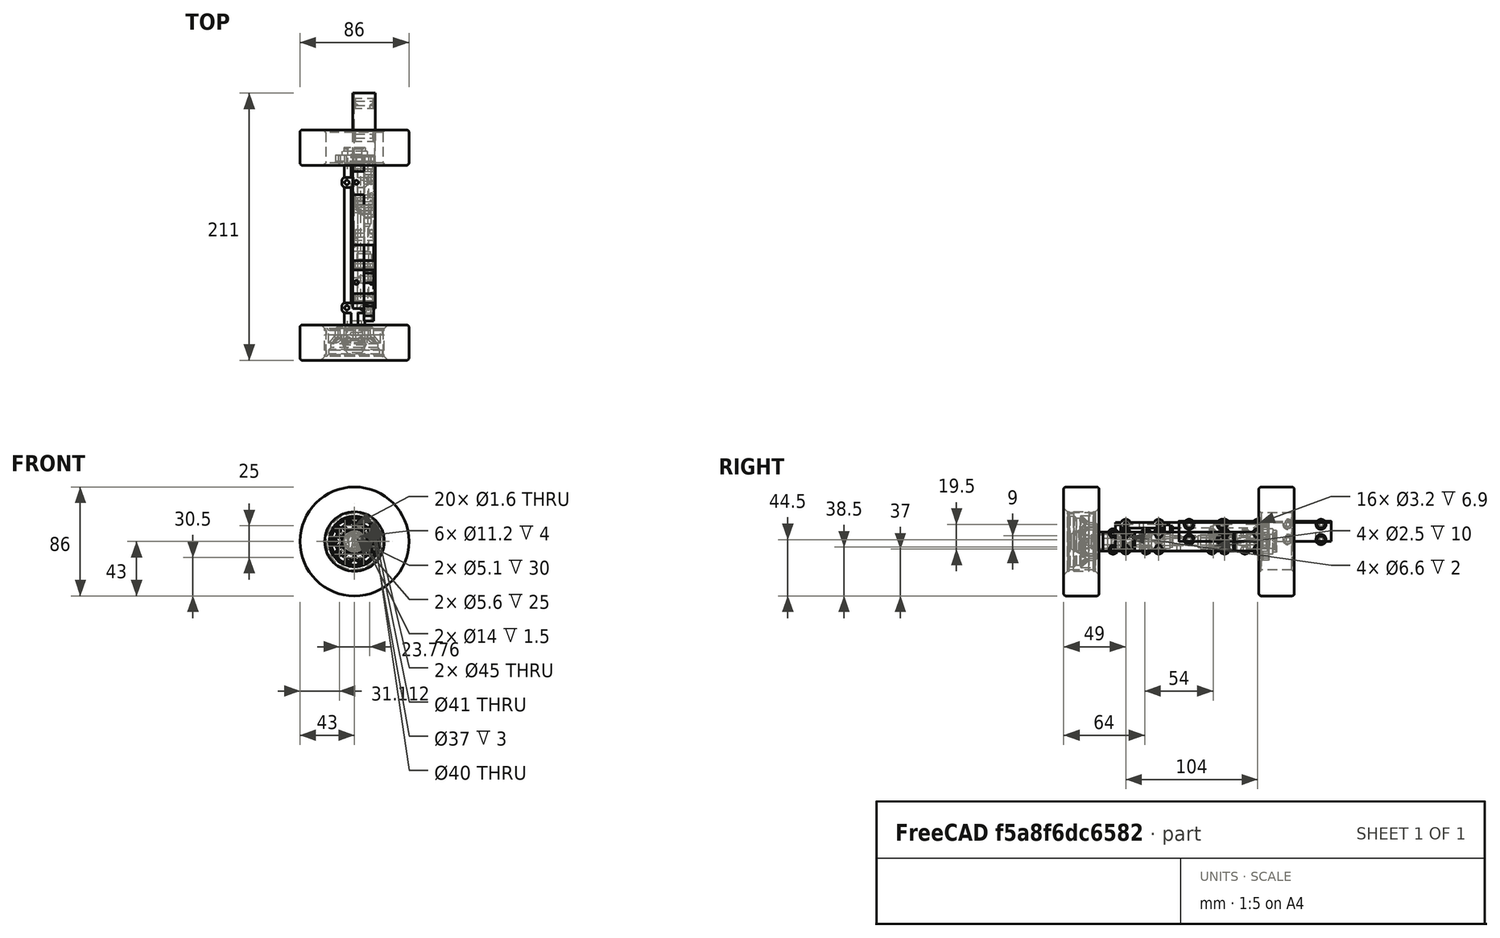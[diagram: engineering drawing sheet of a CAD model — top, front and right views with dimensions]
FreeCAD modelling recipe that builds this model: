
FCSTD DOCUMENT  (FreeCAD 0.19R)
Label: trailer-axle
License: CC-BY 3.0
LicenseURL: http://creativecommons.org/licenses/by/3.0/
objects: Part::Cylinder×133, Part::MultiFuse×123, Part::Cut×40, Part::Box×11, Part::Fillet×10, Part::Extrusion×8, Part::Chamfer×8, Part::Mirroring×5, Part::Feature×4, Part::Cone×3
note: 345 computed .brp shape members not serialized (recipe doc carries the construction recipe); baked Part::Feature solids carry a one-line shape summary decoded from their .brp

FEATURE [Part::Box] Box
  AttacherType = Attacher::AttachEngine3D
  Height = 15
  Length = 18
  Placement = pos=(-1.5,0,0) rot=(0,0,1;0rad)
  Width = 120
FEATURE [Part::Cylinder] Cylinder
  Angle = 360
  AttacherType = Attacher::AttachEngine3D
  Height = 18
  Placement = pos=(0,8,1.5) rot=(0,1,0;1.5708rad)
  Radius = 4
FEATURE [Part::Cylinder] Cylinder001
  Angle = 360
  AttacherType = Attacher::AttachEngine3D
  Height = 18
  Placement = pos=(0,8,13.5) rot=(0,1,0;1.5708rad)
  Radius = 4
FEATURE [Part::Cylinder] Cylinder002
  Angle = 360
  AttacherType = Attacher::AttachEngine3D
  Height = 18
  Placement = pos=(0,8,1.5) rot=(0,1,0;1.5708rad)
  Radius = 4
FEATURE [Part::Cylinder] Cylinder003
  Angle = 360
  AttacherType = Attacher::AttachEngine3D
  Height = 18
  Placement = pos=(0,8,13.5) rot=(0,1,0;1.5708rad)
  Radius = 4
FEATURE [Part::MultiFuse] Fusion009
  Refine = true
  Shapes = -> [Cylinder,Cylinder001]
FEATURE [Part::MultiFuse] Fusion010
  Placement = pos=(0,104,0) rot=(0,0,1;0rad)
  Refine = true
  Shapes = -> [Cylinder002,Cylinder003]
FEATURE [Part::MultiFuse] Fusion008
  Placement = pos=(-1.5,0,0) rot=(0,0,1;0rad)
  Refine = true
  Shapes = -> [Fusion009,Fusion010]
FEATURE [Part::Cylinder] Cylinder004
  Angle = 360
  AttacherType = Attacher::AttachEngine3D
  Height = 18
  Placement = pos=(0,8,1.5) rot=(0,1,0;1.5708rad)
  Radius = 1.6
FEATURE [Part::Cylinder] Cylinder005
  Angle = 360
  AttacherType = Attacher::AttachEngine3D
  Height = 18
  Placement = pos=(0,8,13.5) rot=(0,1,0;1.5708rad)
  Radius = 1.6
FEATURE [Part::Cylinder] Cylinder006
  Angle = 360
  AttacherType = Attacher::AttachEngine3D
  Height = 18
  Placement = pos=(0,8,1.5) rot=(0,1,0;1.5708rad)
  Radius = 1.6
FEATURE [Part::Cylinder] Cylinder007
  Angle = 360
  AttacherType = Attacher::AttachEngine3D
  Height = 18
  Placement = pos=(0,8,13.5) rot=(0,1,0;1.5708rad)
  Radius = 1.6
FEATURE [Part::MultiFuse] Fusion012
  Refine = true
  Shapes = -> [Cylinder004,Cylinder005]
FEATURE [Part::MultiFuse] Fusion013
  Placement = pos=(0,104,0) rot=(0,0,1;0rad)
  Refine = true
  Shapes = -> [Cylinder006,Cylinder007]
FEATURE [Part::MultiFuse] Fusion014
  Placement = pos=(-1.5,0,0) rot=(0,0,1;0rad)
  Refine = true
  Shapes = -> [Fusion012,Fusion013]
FEATURE [Part::Cylinder] Cylinder008
  Angle = 360
  AttacherType = Attacher::AttachEngine3D
  Height = 2
  Placement = pos=(0,8,1.5) rot=(0,1,0;1.5708rad)
  Radius = 3.3
FEATURE [Part::Cylinder] Cylinder009
  Angle = 360
  AttacherType = Attacher::AttachEngine3D
  Height = 2
  Placement = pos=(0,8,13.5) rot=(0,1,0;1.5708rad)
  Radius = 3.1
FEATURE [Part::MultiFuse] Fusion015
  Refine = true
  Shapes = -> [Cylinder009,Cylinder008]
FEATURE [Part::Cylinder] Cylinder010
  Angle = 360
  AttacherType = Attacher::AttachEngine3D
  Height = 2
  Placement = pos=(0,8,13.5) rot=(0,1,0;1.5708rad)
  Radius = 3.1
FEATURE [Part::Cylinder] Cylinder011
  Angle = 360
  AttacherType = Attacher::AttachEngine3D
  Height = 2
  Placement = pos=(0,8,1.5) rot=(0,1,0;1.5708rad)
  Radius = 3.3
FEATURE [Part::MultiFuse] Fusion016
  Placement = pos=(0,104,0) rot=(0,0,1;0rad)
  Refine = true
  Shapes = -> [Cylinder010,Cylinder011]
FEATURE [Part::MultiFuse] Fusion018
  Placement = pos=(-1.5,0,0) rot=(0,0,1;0rad)
  Refine = true
  Shapes = -> [Fusion015,Fusion016]
FEATURE [Part::Feature] Face
  Placement = pos=(-1,8,1.5) rot=(0.250563,0.935113,0.250563;1.63783rad)
  shape: bbox 2e-07 x 9.017 x 9.331 mm, 1 faces, 0 solids (baked)
FEATURE [Part::Extrusion] Extrude
  Base = -> Face
  Dir = (2,0,0)
  DirMode = 0
  FaceMakerClass = Part::FaceMakerExtrusion
  LengthFwd = 0
  LengthRev = 0
  Placement = pos=(-2,0,0) rot=(0,0,1;0rad)
  Solid = false
  Symmetric = false
FEATURE [Part::Feature] Face001
  Placement = pos=(-1,8,1.5) rot=(0.250563,0.935113,0.250563;1.63783rad)
  shape: bbox 2e-07 x 9.017 x 9.331 mm, 1 faces, 0 solids (baked)
FEATURE [Part::Extrusion] Extrude001
  Base = -> Face001
  Dir = (2,0,0)
  DirMode = 0
  FaceMakerClass = Part::FaceMakerExtrusion
  LengthFwd = 0
  LengthRev = 0
  Placement = pos=(-2,0,12) rot=(0,0,1;0rad)
  Solid = false
  Symmetric = false
FEATURE [Part::MultiFuse] Fusion019
  Refine = true
  Shapes = -> [Extrude001,Extrude]
FEATURE [Part::Extrusion] Extrude002
  Base = -> Face
  Dir = (2,0,0)
  DirMode = 0
  FaceMakerClass = Part::FaceMakerExtrusion
  LengthFwd = 0
  LengthRev = 0
  Placement = pos=(-2,0,0) rot=(0,0,1;0rad)
  Solid = false
  Symmetric = false
FEATURE [Part::Extrusion] Extrude003
  Base = -> Face001
  Dir = (2,0,0)
  DirMode = 0
  FaceMakerClass = Part::FaceMakerExtrusion
  LengthFwd = 0
  LengthRev = 0
  Placement = pos=(-2,0,12) rot=(0,0,1;0rad)
  Solid = false
  Symmetric = false
FEATURE [Part::MultiFuse] Fusion020
  Placement = pos=(0,104,0) rot=(0,0,1;0rad)
  Refine = true
  Shapes = -> [Extrude003,Extrude002]
FEATURE [Part::MultiFuse] Fusion021
  Placement = pos=(1.5,0,0) rot=(0,0,1;0rad)
  Refine = true
  Shapes = -> [Fusion020,Fusion019]
FEATURE [Part::Cylinder] Cylinder014
  Angle = 360
  AttacherType = Attacher::AttachEngine3D
  Height = 15
  Placement = pos=(12,0,0) rot=(0,0,1;0rad)
  Radius = 1.6
FEATURE [Part::Cylinder] Cylinder015
  Angle = 360
  AttacherType = Attacher::AttachEngine3D
  Height = 15
  Radius = 1.6
FEATURE [Part::MultiFuse] Fusion024
  Placement = pos=(1.5,20.5,0) rot=(0,0,1;0rad)
  Refine = true
  Shapes = -> [Cylinder014,Cylinder015]
FEATURE [Part::Cylinder] Cylinder018
  Angle = 360
  AttacherType = Attacher::AttachEngine3D
  Height = 15
  Placement = pos=(12,0,0) rot=(0,0,1;0rad)
  Radius = 1.6
FEATURE [Part::Cylinder] Cylinder019
  Angle = 360
  AttacherType = Attacher::AttachEngine3D
  Height = 15
  Radius = 1.6
FEATURE [Part::MultiFuse] Fusion030
  Placement = pos=(1.5,99.5,0) rot=(0,0,1;0rad)
  Refine = true
  Shapes = -> [Cylinder018,Cylinder019]
FEATURE [Part::MultiFuse] Fusion031
  Refine = true
  Shapes = -> [Fusion024,Fusion030]
FEATURE [Part::MultiFuse] Fusion032
  Placement = pos=(0,78,0) rot=(0,0,1;0rad)
  Refine = true
  Shapes = -> [Extrude003,Extrude002]
FEATURE [Part::MultiFuse] Fusion034
  Placement = pos=(0,26,0) rot=(0,0,1;0rad)
  Refine = true
  Shapes = -> [Extrude001,Extrude]
FEATURE [Part::MultiFuse] Fusion035
  Placement = pos=(0,26,0) rot=(0,0,1;0rad)
  Refine = true
  Shapes = -> [Cylinder009,Cylinder008]
FEATURE [Part::MultiFuse] Fusion036
  Placement = pos=(0,78,0) rot=(0,0,1;0rad)
  Refine = true
  Shapes = -> [Cylinder010,Cylinder011]
FEATURE [Part::MultiFuse] Fusion037
  Placement = pos=(-1.5,0,0) rot=(0,0,1;0rad)
  Refine = true
  Shapes = -> [Fusion035,Fusion036]
FEATURE [Part::MultiFuse] Fusion038
  Placement = pos=(1.5,0,0) rot=(0,0,1;0rad)
  Refine = true
  Shapes = -> [Fusion032,Fusion034]
FEATURE [Part::MultiFuse] Fusion039
  Placement = pos=(0,26,0) rot=(0,0,1;0rad)
  Refine = true
  Shapes = -> [Cylinder,Cylinder001]
FEATURE [Part::MultiFuse] Fusion040
  Placement = pos=(0,78,0) rot=(0,0,1;0rad)
  Refine = true
  Shapes = -> [Cylinder002,Cylinder003]
FEATURE [Part::MultiFuse] Fusion041
  Placement = pos=(-1.5,0,0) rot=(0,0,1;0rad)
  Refine = true
  Shapes = -> [Fusion040,Fusion039]
FEATURE [Part::MultiFuse] Fusion043
  Placement = pos=(0,78,0) rot=(0,0,1;0rad)
  Refine = true
  Shapes = -> [Cylinder006,Cylinder007]
FEATURE [Part::MultiFuse] Fusion044
  Placement = pos=(0,26,0) rot=(0,0,1;0rad)
  Refine = true
  Shapes = -> [Cylinder004,Cylinder005]
FEATURE [Part::MultiFuse] Fusion045
  Placement = pos=(-1.5,0,0) rot=(0,0,1;0rad)
  Refine = true
  Shapes = -> [Fusion043,Fusion044]
FEATURE [Part::Cylinder] Cylinder020
  Angle = 360
  AttacherType = Attacher::AttachEngine3D
  Height = 130
  Placement = pos=(7.5,125,7.5) rot=(1,0,0;1.5708rad)
  Radius = 3.5
FEATURE [Part::Cut] Cut008
  Refine = true
  Tool = -> Cylinder020
FEATURE [Part::Cylinder] Cylinder021
  Angle = 360
  AttacherType = Attacher::AttachEngine3D
  Height = 4
  Placement = pos=(7.5,4,20) rot=(1,0,0;1.5708rad)
  Radius = 5.6
FEATURE [Part::Cylinder] Cylinder022
  Angle = 360
  AttacherType = Attacher::AttachEngine3D
  Height = 2
  Placement = pos=(7.5,45,20) rot=(1,0,0;1.5708rad)
  Radius = 4.7
FEATURE [Part::Cylinder] Cylinder023
  Angle = 360
  AttacherType = Attacher::AttachEngine3D
  Height = 4.5
  Placement = pos=(7.5,43,20) rot=(1,0,0;1.5708rad)
  Radius = 5.6
FEATURE [Part::MultiFuse] Fusion047
  Refine = true
  Shapes = -> [Cylinder021,Cylinder023,Cylinder022]
FEATURE [Part::Cylinder] Cylinder024
  Angle = 360
  AttacherType = Attacher::AttachEngine3D
  Height = 2
  Placement = pos=(7.5,45,20) rot=(1,0,0;1.5708rad)
  Radius = 4.7
FEATURE [Part::Cylinder] Cylinder025
  Angle = 360
  AttacherType = Attacher::AttachEngine3D
  Height = 4
  Placement = pos=(7.5,4,20) rot=(1,0,0;1.5708rad)
  Radius = 5.6
FEATURE [Part::Cylinder] Cylinder026
  Angle = 360
  AttacherType = Attacher::AttachEngine3D
  Height = 4.5
  Placement = pos=(7.5,43,20) rot=(1,0,0;1.5708rad)
  Radius = 5.6
FEATURE [Part::MultiFuse] Fusion048
  Placement = pos=(15,120,0) rot=(0,0,1;3.14159rad)
  Refine = true
  Shapes = -> [Cylinder025,Cylinder026,Cylinder024]
FEATURE [Part::MultiFuse] Fusion049
  Placement = pos=(0,0,-12.5) rot=(0,0,1;0rad)
  Refine = true
  Shapes = -> [Fusion047,Fusion048]
FEATURE [Part::Cut] Cut009
  Base = -> Cut008
  Refine = true
  Tool = -> Fusion049
FEATURE [Part::Box] Box007
  AttacherType = Attacher::AttachEngine3D
  Height = 30
  Length = 10
  Placement = pos=(-2.5,0,-7) rot=(0,0,1;0rad)
  Width = 120
FEATURE [Part::Box] Box008
  AttacherType = Attacher::AttachEngine3D
  Height = 30
  Length = 10
  Placement = pos=(7.5,0,-7) rot=(0,0,1;0rad)
  Width = 120
FEATURE [Part::MultiFuse] Fusion050
  Placement = pos=(0,0,-12.5) rot=(0,0,1;0rad)
  Refine = true
  Shapes = -> [Fusion047,Fusion048]
FEATURE [Part::Cut] Cut012
  Base = -> Cut009
  Placement = pos=(0,-60,-7.5) rot=(0,0,1;0rad)
  Refine = true
  Tool = -> Box007
FEATURE [Part::Cut] Cut
  Base = -> Box
  Refine = true
  Tool = -> Fusion031
FEATURE [Part::MultiFuse] Fusion
  Refine = true
  Shapes = -> [Fusion041,Fusion008,Cut]
FEATURE [Part::MultiFuse] Fusion051
  Refine = true
  Shapes = -> [Fusion014,Fusion045]
FEATURE [Part::MultiFuse] Fusion052
  Refine = true
  Shapes = -> [Fusion018,Fusion021,Fusion037,Fusion038]
FEATURE [Part::MultiFuse] Fusion053
  Refine = true
  Shapes = -> [Fusion051,Fusion052]
FEATURE [Part::Cut] Cut013
  Base = -> Fusion
  Refine = true
  Tool = -> Fusion053
FEATURE [Part::Cylinder] Cylinder027
  Angle = 360
  AttacherType = Attacher::AttachEngine3D
  Height = 120
  Placement = pos=(7.5,120,7.5) rot=(1,0,0;1.5708rad)
  Radius = 3
FEATURE [Part::MultiFuse] Fusion054
  Refine = true
  Shapes = -> [Cylinder027,Fusion050]
FEATURE [Part::Cut] Cut014
  Base = -> Cut013
  Refine = true
  Tool = -> Fusion054
FEATURE [Part::MultiFuse] Fusion055
  Refine = true
  Shapes = -> [Cylinder027,Fusion050]
FEATURE [Part::Cut] Cut016
  Base = -> Fusion
  Refine = true
  Tool = -> Fusion053
FEATURE [Part::Cut] Cut015
  Base = -> Cut016
  Refine = true
  Tool = -> Fusion055
FEATURE [Part::Box] Box009
  AttacherType = Attacher::AttachEngine3D
  Height = 30
  Length = 10
  Placement = pos=(-2.5,0,-7) rot=(0,0,1;0rad)
  Width = 120
FEATURE [Part::Cut] Cut017
  Base = -> Cut014
  Refine = true
  Tool = -> Box008
FEATURE [Part::Cut] Cut018
  Base = -> Cut015
  Refine = true
  Tool = -> Box009
FEATURE [Part::Cylinder] Cylinder028
  Angle = 360
  AttacherType = Attacher::AttachEngine3D
  Height = 0.1
  Placement = pos=(0.5,8,1.5) rot=(0,1,0;1.5708rad)
  Radius = 1.6
FEATURE [Part::Cylinder] Cylinder029
  Angle = 360
  AttacherType = Attacher::AttachEngine3D
  Height = 0.1
  Placement = pos=(0.5,8,13.5) rot=(0,1,0;1.5708rad)
  Radius = 1.6
FEATURE [Part::MultiFuse] Fusion056
  Refine = true
  Shapes = -> [Cylinder029,Cylinder028]
FEATURE [Part::Cylinder] Cylinder030
  Angle = 360
  AttacherType = Attacher::AttachEngine3D
  Height = 0.1
  Placement = pos=(0.5,8,13.5) rot=(0,1,0;1.5708rad)
  Radius = 1.6
FEATURE [Part::Cylinder] Cylinder031
  Angle = 360
  AttacherType = Attacher::AttachEngine3D
  Height = 0.1
  Placement = pos=(0.5,8,1.5) rot=(0,1,0;1.5708rad)
  Radius = 1.6
FEATURE [Part::MultiFuse] Fusion057
  Placement = pos=(0,26,0) rot=(0,0,1;0rad)
  Refine = true
  Shapes = -> [Cylinder030,Cylinder031]
FEATURE [Part::MultiFuse] Fusion058
  Refine = true
  Shapes = -> [Fusion056,Fusion057]
FEATURE [Part::MultiFuse] Fusion059
  Placement = pos=(0,26,0) rot=(0,0,1;0rad)
  Refine = true
  Shapes = -> [Cylinder030,Cylinder031]
FEATURE [Part::MultiFuse] Fusion060
  Refine = true
  Shapes = -> [Cylinder029,Cylinder028]
FEATURE [Part::MultiFuse] Fusion061
  Placement = pos=(0,78,0) rot=(0,0,1;0rad)
  Refine = true
  Shapes = -> [Fusion060,Fusion059]
FEATURE [Part::MultiFuse] Fusion062
  Refine = true
  Shapes = -> [Fusion061,Fusion058]
FEATURE [Part::MultiFuse] Fusion063
  Refine = true
  Shapes = -> [Fusion056,Fusion057]
FEATURE [Part::MultiFuse] Fusion065
  Placement = pos=(0,78,0) rot=(0,0,1;0rad)
  Refine = true
  Shapes = -> [Fusion060,Fusion059]
FEATURE [Part::MultiFuse] Fusion064
  Placement = pos=(13.9,0,0) rot=(0,0,1;0rad)
  Refine = true
  Shapes = -> [Fusion065,Fusion063]
FEATURE [Part::MultiFuse] Fusion066
  Placement = pos=(0,-50,0) rot=(0,0,1;0rad)
  Refine = true
  Shapes = -> [Cut017,Fusion062]
FEATURE [Part::MultiFuse] Fusion067
  Placement = pos=(0,-50,-7.5) rot=(0,0,1;0rad)
  Refine = true
  Shapes = -> [Fusion064,Cut018]
FEATURE [Part::Cylinder] Cylinder032
  Angle = 360
  AttacherType = Attacher::AttachEngine3D
  Height = 15
  Placement = pos=(12,0,0) rot=(0,0,1;0rad)
  Radius = 1.6
FEATURE [Part::Cylinder] Cylinder033
  Angle = 360
  AttacherType = Attacher::AttachEngine3D
  Height = 15
  Radius = 1.6
FEATURE [Part::MultiFuse] Fusion068
  Placement = pos=(1.5,10.5,0) rot=(0,0,1;0rad)
  Refine = true
  Shapes = -> [Cylinder032,Cylinder033]
FEATURE [Part::Cylinder] Cylinder034
  Angle = 360
  AttacherType = Attacher::AttachEngine3D
  Height = 15
  Placement = pos=(12,0,0) rot=(0,0,1;0rad)
  Radius = 1.6
FEATURE [Part::Cylinder] Cylinder035
  Angle = 360
  AttacherType = Attacher::AttachEngine3D
  Height = 15
  Radius = 1.6
FEATURE [Part::MultiFuse] Fusion069
  Placement = pos=(1.5,109.5,0) rot=(0,0,1;0rad)
  Refine = true
  Shapes = -> [Cylinder034,Cylinder035]
FEATURE [Part::Feature] Face002
  Placement = pos=(-1,8,1.5) rot=(0.250563,0.935113,0.250563;1.63783rad)
  shape: bbox 2e-07 x 9.017 x 9.331 mm, 1 faces, 0 solids (baked)
FEATURE [Part::Cylinder] Cylinder036
  Angle = 360
  AttacherType = Attacher::AttachEngine3D
  Height = 18
  Placement = pos=(0,8,1.5) rot=(0,1,0;1.5708rad)
  Radius = 1.6
FEATURE [Part::Cylinder] Cylinder037
  Angle = 360
  AttacherType = Attacher::AttachEngine3D
  Height = 18
  Placement = pos=(0,8,13.5) rot=(0,1,0;1.5708rad)
  Radius = 1.6
FEATURE [Part::MultiFuse] Fusion072
  Refine = true
  Shapes = -> [Cylinder036,Cylinder037]
FEATURE [Part::Cylinder] Cylinder038
  Angle = 360
  AttacherType = Attacher::AttachEngine3D
  Height = 18
  Placement = pos=(0,8,1.5) rot=(0,1,0;1.5708rad)
  Radius = 1.6
FEATURE [Part::Cylinder] Cylinder039
  Angle = 360
  AttacherType = Attacher::AttachEngine3D
  Height = 18
  Placement = pos=(0,8,13.5) rot=(0,1,0;1.5708rad)
  Radius = 1.6
FEATURE [Part::MultiFuse] Fusion073
  Placement = pos=(0,104,0) rot=(0,0,1;0rad)
  Refine = true
  Shapes = -> [Cylinder038,Cylinder039]
FEATURE [Part::MultiFuse] Fusion070
  Placement = pos=(-1.5,0,0) rot=(0,0,1;0rad)
  Refine = true
  Shapes = -> [Fusion072,Fusion073]
FEATURE [Part::Cylinder] Cylinder040
  Angle = 360
  AttacherType = Attacher::AttachEngine3D
  Height = 2
  Placement = pos=(0,8,1.5) rot=(0,1,0;1.5708rad)
  Radius = 3.3
FEATURE [Part::Cylinder] Cylinder041
  Angle = 360
  AttacherType = Attacher::AttachEngine3D
  Height = 2
  Placement = pos=(0,8,13.5) rot=(0,1,0;1.5708rad)
  Radius = 3.1
FEATURE [Part::MultiFuse] Fusion071
  Refine = true
  Shapes = -> [Cylinder041,Cylinder040]
FEATURE [Part::Cylinder] Cylinder042
  Angle = 360
  AttacherType = Attacher::AttachEngine3D
  Height = 2
  Placement = pos=(0,8,13.5) rot=(0,1,0;1.5708rad)
  Radius = 3.1
FEATURE [Part::Cylinder] Cylinder043
  Angle = 360
  AttacherType = Attacher::AttachEngine3D
  Height = 2
  Placement = pos=(0,8,1.5) rot=(0,1,0;1.5708rad)
  Radius = 3.3
FEATURE [Part::MultiFuse] Fusion074
  Placement = pos=(0,104,0) rot=(0,0,1;0rad)
  Refine = true
  Shapes = -> [Cylinder042,Cylinder043]
FEATURE [Part::MultiFuse] Fusion075
  Placement = pos=(-1.5,0,0) rot=(0,0,1;0rad)
  Refine = true
  Shapes = -> [Fusion071,Fusion074]
FEATURE [Part::Extrusion] Extrude004
  Base = -> Face002
  Dir = (2,0,0)
  DirMode = 0
  FaceMakerClass = Part::FaceMakerExtrusion
  LengthFwd = 0
  LengthRev = 0
  Placement = pos=(-2,0,0) rot=(0,0,1;0rad)
  Solid = false
  Symmetric = false
FEATURE [Part::Feature] Face003
  Placement = pos=(-1,8,1.5) rot=(0.250563,0.935113,0.250563;1.63783rad)
  shape: bbox 2e-07 x 9.017 x 9.331 mm, 1 faces, 0 solids (baked)
FEATURE [Part::Extrusion] Extrude005
  Base = -> Face003
  Dir = (2,0,0)
  DirMode = 0
  FaceMakerClass = Part::FaceMakerExtrusion
  LengthFwd = 0
  LengthRev = 0
  Placement = pos=(-2,0,12) rot=(0,0,1;0rad)
  Solid = false
  Symmetric = false
FEATURE [Part::MultiFuse] Fusion076
  Refine = true
  Shapes = -> [Extrude005,Extrude004]
FEATURE [Part::Extrusion] Extrude006
  Base = -> Face002
  Dir = (2,0,0)
  DirMode = 0
  FaceMakerClass = Part::FaceMakerExtrusion
  LengthFwd = 0
  LengthRev = 0
  Placement = pos=(-2,0,0) rot=(0,0,1;0rad)
  Solid = false
  Symmetric = false
FEATURE [Part::Extrusion] Extrude007
  Base = -> Face003
  Dir = (2,0,0)
  DirMode = 0
  FaceMakerClass = Part::FaceMakerExtrusion
  LengthFwd = 0
  LengthRev = 0
  Placement = pos=(-2,0,12) rot=(0,0,1;0rad)
  Solid = false
  Symmetric = false
FEATURE [Part::MultiFuse] Fusion077
  Placement = pos=(0,104,0) rot=(0,0,1;0rad)
  Refine = true
  Shapes = -> [Extrude007,Extrude006]
FEATURE [Part::MultiFuse] Fusion078
  Placement = pos=(1.5,0,0) rot=(0,0,1;0rad)
  Refine = true
  Shapes = -> [Fusion077,Fusion076]
FEATURE [Part::MultiFuse] Fusion079
  Placement = pos=(0,78,0) rot=(0,0,1;0rad)
  Refine = true
  Shapes = -> [Extrude007,Extrude006]
FEATURE [Part::MultiFuse] Fusion080
  Placement = pos=(0,26,0) rot=(0,0,1;0rad)
  Refine = true
  Shapes = -> [Extrude005,Extrude004]
FEATURE [Part::MultiFuse] Fusion081
  Placement = pos=(0,26,0) rot=(0,0,1;0rad)
  Refine = true
  Shapes = -> [Cylinder041,Cylinder040]
FEATURE [Part::MultiFuse] Fusion082
  Placement = pos=(0,78,0) rot=(0,0,1;0rad)
  Refine = true
  Shapes = -> [Cylinder042,Cylinder043]
FEATURE [Part::MultiFuse] Fusion083
  Placement = pos=(-1.5,0,0) rot=(0,0,1;0rad)
  Refine = true
  Shapes = -> [Fusion081,Fusion082]
FEATURE [Part::MultiFuse] Fusion084
  Placement = pos=(1.5,0,0) rot=(0,0,1;0rad)
  Refine = true
  Shapes = -> [Fusion079,Fusion080]
FEATURE [Part::MultiFuse] Fusion085
  Placement = pos=(0,78,0) rot=(0,0,1;0rad)
  Refine = true
  Shapes = -> [Cylinder038,Cylinder039]
FEATURE [Part::MultiFuse] Fusion086
  Placement = pos=(0,26,0) rot=(0,0,1;0rad)
  Refine = true
  Shapes = -> [Cylinder036,Cylinder037]
FEATURE [Part::MultiFuse] Fusion087
  Placement = pos=(-1.5,0,0) rot=(0,0,1;0rad)
  Refine = true
  Shapes = -> [Fusion085,Fusion086]
FEATURE [Part::MultiFuse] Fusion088
  Refine = true
  Shapes = -> [Fusion070,Fusion087]
FEATURE [Part::MultiFuse] Fusion089
  Refine = true
  Shapes = -> [Fusion075,Fusion078,Fusion083,Fusion084]
FEATURE [Part::MultiFuse] Fusion090
  Refine = true
  Shapes = -> [Fusion088,Fusion089]
FEATURE [Part::Cylinder] Cylinder044
  Angle = 360
  AttacherType = Attacher::AttachEngine3D
  Height = 18
  Placement = pos=(0,8,1.5) rot=(0,1,0;1.5708rad)
  Radius = 4
FEATURE [Part::Cylinder] Cylinder045
  Angle = 360
  AttacherType = Attacher::AttachEngine3D
  Height = 18
  Placement = pos=(0,8,13.5) rot=(0,1,0;1.5708rad)
  Radius = 4
FEATURE [Part::MultiFuse] Fusion093
  Refine = true
  Shapes = -> [Cylinder044,Cylinder045]
FEATURE [Part::Cylinder] Cylinder046
  Angle = 360
  AttacherType = Attacher::AttachEngine3D
  Height = 18
  Placement = pos=(0,8,1.5) rot=(0,1,0;1.5708rad)
  Radius = 4
FEATURE [Part::Cylinder] Cylinder047
  Angle = 360
  AttacherType = Attacher::AttachEngine3D
  Height = 18
  Placement = pos=(0,8,13.5) rot=(0,1,0;1.5708rad)
  Radius = 4
FEATURE [Part::MultiFuse] Fusion092
  Placement = pos=(0,104,0) rot=(0,0,1;0rad)
  Refine = true
  Shapes = -> [Cylinder046,Cylinder047]
FEATURE [Part::MultiFuse] Fusion091
  Placement = pos=(-1.5,0,0) rot=(0,0,1;0rad)
  Refine = true
  Shapes = -> [Fusion093,Fusion092]
FEATURE [Part::MultiFuse] Fusion094
  Placement = pos=(0,26,0) rot=(0,0,1;0rad)
  Refine = true
  Shapes = -> [Cylinder044,Cylinder045]
FEATURE [Part::MultiFuse] Fusion095
  Placement = pos=(0,78,0) rot=(0,0,1;0rad)
  Refine = true
  Shapes = -> [Cylinder046,Cylinder047]
FEATURE [Part::MultiFuse] Fusion096
  Placement = pos=(-1.5,0,0) rot=(0,0,1;0rad)
  Refine = true
  Shapes = -> [Fusion095,Fusion094]
FEATURE [Part::Box] Box010
  AttacherType = Attacher::AttachEngine3D
  Height = 15
  Length = 18
  Placement = pos=(-1.5,0,0) rot=(0,0,1;0rad)
  Width = 120
FEATURE [Part::Cylinder] Cylinder048
  Angle = 360
  AttacherType = Attacher::AttachEngine3D
  Height = 120
  Placement = pos=(8,0,8) rot=(-1,0,0;1.5708rad)
  Radius = 8
FEATURE [Part::Cylinder] Cylinder049
  Angle = 360
  AttacherType = Attacher::AttachEngine3D
  Height = 28
  Placement = pos=(0,0,0) rot=(1,0,0;1.5708rad)
  Radius = 43
FEATURE [Part::Cylinder] Cylinder050
  Angle = 360
  AttacherType = Attacher::AttachEngine3D
  Height = 28
  Placement = pos=(0,0,0) rot=(1,0,0;1.5708rad)
  Radius = 22.5
FEATURE [Part::Cut] Cut019
  Base = -> Cylinder049
  Refine = true
  Tool = -> Cylinder050
FEATURE [Part::Cylinder] Cylinder051
  Angle = 360
  AttacherType = Attacher::AttachEngine3D
  Height = 28
  Placement = pos=(0,0,0) rot=(1,0,0;1.5708rad)
  Radius = 43
FEATURE [Part::Cylinder] Cylinder052
  Angle = 360
  AttacherType = Attacher::AttachEngine3D
  Height = 28
  Placement = pos=(0,0,0) rot=(1,0,0;1.5708rad)
  Radius = 22.5
FEATURE [Part::Cut] Cut020
  Base = -> Cylinder051
  Refine = true
  Tool = -> Cylinder052
FEATURE [Part::Fillet] Fillet003
  Base = -> Cut020
  Edges = 2 edges r=2: [Edge1,Edge3]
FEATURE [Part::Chamfer] Chamfer001
  Base = -> Fillet003
  Edges = 2 edges r=2: [Edge8,Edge9]
FEATURE [Part::Fillet] Fillet002  label="wheel-wide-right"
  Base = -> Chamfer001
  Edges = 2 edges r=3: [Edge1,Edge12]
  Placement = pos=(0,91,0) rot=(0,0,1;0rad)
FEATURE [Part::Cylinder] Cylinder073
  Angle = 360
  AttacherType = Attacher::AttachEngine3D
  Height = 22
  Radius = 23.5
FEATURE [Part::Cone] Cone002
  Angle = 360
  AttacherType = Attacher::AttachEngine3D
  Height = 7
  Placement = pos=(0,0,15) rot=(0,0,1;0rad)
  Radius1 = 21
  Radius2 = 15
FEATURE [Part::Cylinder] Cylinder081
  Angle = 360
  AttacherType = Attacher::AttachEngine3D
  Height = 26
  Radius = 10
FEATURE [Part::Cylinder] Cylinder078
  Angle = 360
  AttacherType = Attacher::AttachEngine3D
  Height = 22
  Radius = 18.5
FEATURE [Part::Cylinder] Cylinder074
  Angle = 360
  AttacherType = Attacher::AttachEngine3D
  Height = 19
  Radius = 23.5
FEATURE [Part::Cut] Cut027
  Base = -> Cone002
  Refine = true
  Tool = -> Cylinder081
FEATURE [Part::Cylinder] Cylinder077
  Angle = 360
  AttacherType = Attacher::AttachEngine3D
  Height = 12
  Placement = pos=(0,0,0.5) rot=(0,0,1;0rad)
  Radius = 23.5
FEATURE [Part::Cylinder] Cylinder084
  Angle = 360
  AttacherType = Attacher::AttachEngine3D
  Height = 8
  Placement = pos=(12,0,16) rot=(0,1,0;1.01229rad)
  Radius = 2.5
FEATURE [Part::Cylinder] Cylinder085
  Angle = 360
  AttacherType = Attacher::AttachEngine3D
  Height = 8
  Placement = pos=(12,0,16) rot=(0,1,0;1.01229rad)
  Radius = 2.5
FEATURE [Part::Mirroring] Part__Mirroring006  label="Cylinder107 (Mirror #1)010"
  Base = (0,0,0)
  Normal = (0,0,1)
  Source = -> Cylinder085
FEATURE [Part::MultiFuse] Fusion097
  Placement = pos=(0,0,0) rot=(0,0,1;0.628319rad)
  Refine = true
  Shapes = -> [Cylinder084,Part__Mirroring006]
FEATURE [Part::Cylinder] Cylinder075
  Angle = 360
  AttacherType = Attacher::AttachEngine3D
  Height = 19
  Radius = 22.1
FEATURE [Part::Cut] Cut022
  Base = -> Cylinder074
  Placement = pos=(0,0,1.5) rot=(0,0,1;0rad)
  Refine = true
  Tool = -> Cylinder075
FEATURE [Part::Cut] Cut023
  Base = -> Cylinder073
  Refine = true
  Tool = -> Cut022
FEATURE [Part::Cylinder] Cylinder076
  Angle = 360
  AttacherType = Attacher::AttachEngine3D
  Height = 12
  Radius = 22
FEATURE [Part::Cut] Cut024
  Base = -> Cylinder077
  Placement = pos=(0,0,4.5) rot=(0,0,1;0rad)
  Refine = true
  Tool = -> Cylinder076
FEATURE [Part::MultiFuse] Fusion099
  Refine = true
  Shapes = -> [Cut024,Cut023]
FEATURE [Part::Cut] Cut025
  Base = -> Fusion099
  Refine = true
  Tool = -> Cylinder078
FEATURE [Part::Cylinder] Cylinder080
  Angle = 360
  AttacherType = Attacher::AttachEngine3D
  Height = 7
  Radius = 20
FEATURE [Part::Cylinder] Cylinder086
  Angle = 360
  AttacherType = Attacher::AttachEngine3D
  Height = 8
  Placement = pos=(12,0,16) rot=(0,1,0;1.01229rad)
  Radius = 2.5
FEATURE [Part::Cylinder] Cylinder083
  Angle = 360
  AttacherType = Attacher::AttachEngine3D
  Height = 8
  Placement = pos=(12,0,16) rot=(0,1,0;1.01229rad)
  Radius = 2.5
FEATURE [Part::Cylinder] Cylinder079
  Angle = 360
  AttacherType = Attacher::AttachEngine3D
  Height = 12
  Placement = pos=(0,0,10) rot=(0,0,1;0rad)
  Radius = 20.5
FEATURE [Part::Cylinder] Cylinder082
  Angle = 360
  AttacherType = Attacher::AttachEngine3D
  Height = 8
  Placement = pos=(12,0,16) rot=(0,1,0;1.01229rad)
  Radius = 2.5
FEATURE [Part::Mirroring] Part__Mirroring005  label="Cylinder107 (Mirror #1)009"
  Base = (0,0,0)
  Normal = (0,0,1)
  Source = -> Cylinder082
FEATURE [Part::MultiFuse] Fusion098
  Refine = true
  Shapes = -> [Cylinder083,Part__Mirroring005]
FEATURE [Part::Cylinder] Cylinder087
  Angle = 360
  AttacherType = Attacher::AttachEngine3D
  Height = 8
  Placement = pos=(12,0,16) rot=(0,1,0;1.01229rad)
  Radius = 2.5
FEATURE [Part::Mirroring] Part__Mirroring007  label="Cylinder107 (Mirror #1)011"
  Base = (0,0,0)
  Normal = (0,0,1)
  Source = -> Cylinder087
FEATURE [Part::MultiFuse] Fusion017
  Placement = pos=(0,0,0) rot=(0,0,1;1.25664rad)
  Refine = true
  Shapes = -> [Cylinder086,Part__Mirroring007]
FEATURE [Part::Cylinder] Cylinder088
  Angle = 360
  AttacherType = Attacher::AttachEngine3D
  Height = 8
  Placement = pos=(12,0,16) rot=(0,1,0;1.01229rad)
  Radius = 2.5
FEATURE [Part::Cylinder] Cylinder089
  Angle = 360
  AttacherType = Attacher::AttachEngine3D
  Height = 8
  Placement = pos=(12,0,16) rot=(0,1,0;1.01229rad)
  Radius = 2.5
FEATURE [Part::Mirroring] Part__Mirroring008  label="Cylinder107 (Mirror #1)012"
  Base = (0,0,0)
  Normal = (0,0,1)
  Source = -> Cylinder089
FEATURE [Part::MultiFuse] Fusion100
  Placement = pos=(0,0,0) rot=(0,0,1;1.88496rad)
  Refine = true
  Shapes = -> [Cylinder088,Part__Mirroring008]
FEATURE [Part::Cylinder] Cylinder090
  Angle = 360
  AttacherType = Attacher::AttachEngine3D
  Height = 8
  Placement = pos=(12,0,16) rot=(0,1,0;1.01229rad)
  Radius = 2.5
FEATURE [Part::Cylinder] Cylinder091
  Angle = 360
  AttacherType = Attacher::AttachEngine3D
  Height = 8
  Placement = pos=(12,0,16) rot=(0,1,0;1.01229rad)
  Radius = 2.5
FEATURE [Part::Mirroring] Part__Mirroring009  label="Cylinder107 (Mirror #1)013"
  Base = (0,0,0)
  Normal = (0,0,1)
  Source = -> Cylinder091
FEATURE [Part::MultiFuse] Fusion101
  Placement = pos=(0,0,0) rot=(0,0,1;2.51327rad)
  Refine = true
  Shapes = -> [Cylinder090,Part__Mirroring009]
FEATURE [Part::MultiFuse] Fusion102
  Placement = pos=(0,0,-6) rot=(0,0,1;0rad)
  Refine = true
  Shapes = -> [Fusion098,Fusion097,Fusion017,Fusion100,Fusion101]
FEATURE [Part::Cylinder] Cylinder092
  Angle = 360
  AttacherType = Attacher::AttachEngine3D
  Height = 10
  Placement = pos=(12.5,0,13) rot=(0,0,1;0rad)
  Radius = 1.1
FEATURE [Part::Cylinder] Cylinder093
  Angle = 360
  AttacherType = Attacher::AttachEngine3D
  Height = 10
  Placement = pos=(-12.5,0,13) rot=(0,0,1;0rad)
  Radius = 1.1
FEATURE [Part::MultiFuse] Fusion103
  Placement = pos=(0,0,0) rot=(0,0,1;0.314159rad)
  Refine = true
  Shapes = -> [Cylinder092,Cylinder093]
FEATURE [Part::Cylinder] Cylinder094
  Angle = 360
  AttacherType = Attacher::AttachEngine3D
  Height = 10
  Placement = pos=(12.5,0,13) rot=(0,0,1;0rad)
  Radius = 1.1
FEATURE [Part::Cylinder] Cylinder095
  Angle = 360
  AttacherType = Attacher::AttachEngine3D
  Height = 10
  Placement = pos=(-12.5,0,13) rot=(0,0,1;0rad)
  Radius = 1.1
FEATURE [Part::MultiFuse] Fusion022
  Placement = pos=(0,0,0) rot=(0,0,1;0.942478rad)
  Refine = true
  Shapes = -> [Cylinder094,Cylinder095]
FEATURE [Part::Cylinder] Cylinder096
  Angle = 360
  AttacherType = Attacher::AttachEngine3D
  Height = 10
  Placement = pos=(12.5,0,13) rot=(0,0,1;0rad)
  Radius = 1.1
FEATURE [Part::Cylinder] Cylinder097
  Angle = 360
  AttacherType = Attacher::AttachEngine3D
  Height = 10
  Placement = pos=(-12.5,0,13) rot=(0,0,1;0rad)
  Radius = 1.1
FEATURE [Part::MultiFuse] Fusion023
  Placement = pos=(0,0,0) rot=(0,0,1;1.5708rad)
  Refine = true
  Shapes = -> [Cylinder096,Cylinder097]
FEATURE [Part::Cylinder] Cylinder098
  Angle = 360
  AttacherType = Attacher::AttachEngine3D
  Height = 10
  Placement = pos=(12.5,0,13) rot=(0,0,1;0rad)
  Radius = 1.1
FEATURE [Part::Cylinder] Cylinder099
  Angle = 360
  AttacherType = Attacher::AttachEngine3D
  Height = 10
  Placement = pos=(-12.5,0,13) rot=(0,0,1;0rad)
  Radius = 1.1
FEATURE [Part::MultiFuse] Fusion104
  Placement = pos=(0,0,0) rot=(0,0,1;2.19911rad)
  Refine = true
  Shapes = -> [Cylinder098,Cylinder099]
FEATURE [Part::Cylinder] Cylinder100
  Angle = 360
  AttacherType = Attacher::AttachEngine3D
  Height = 10
  Placement = pos=(12.5,0,13) rot=(0,0,1;0rad)
  Radius = 1.1
FEATURE [Part::Cylinder] Cylinder101
  Angle = 360
  AttacherType = Attacher::AttachEngine3D
  Height = 10
  Placement = pos=(-12.5,0,13) rot=(0,0,1;0rad)
  Radius = 1.1
FEATURE [Part::MultiFuse] Fusion025
  Placement = pos=(0,0,0) rot=(0,0,1;2.82743rad)
  Refine = true
  Shapes = -> [Cylinder100,Cylinder101]
FEATURE [Part::MultiFuse] Fusion026
  Placement = pos=(0,0,-5) rot=(0,0,1;0rad)
  Refine = true
  Shapes = -> [Fusion103,Fusion022,Fusion025,Fusion104,Fusion023]
FEATURE [Part::Cone] Cone003
  Angle = 360
  AttacherType = Attacher::AttachEngine3D
  Height = 10
  Placement = pos=(0,0,9) rot=(0,0,1;0rad)
  Radius1 = 24
  Radius2 = 15
FEATURE [Part::Cut] Cut028
  Base = -> Cut027
  Placement = pos=(0,0,-5) rot=(0,0,1;0rad)
  Refine = true
  Tool = -> Cone003
FEATURE [Part::Cut] Cut029
  Base = -> Cut028
  Refine = true
  Tool = -> Fusion102
FEATURE [Part::Cylinder] Cylinder102
  Angle = 360
  AttacherType = Attacher::AttachEngine3D
  Height = 26
  Radius = 10.1
FEATURE [Part::Cut] Cut030
  Base = -> Cut029
  Refine = true
  Tool = -> Fusion026
FEATURE [Part::Cut] Cut031
  Base = -> Cut030
  Refine = true
  Tool = -> Cylinder102
FEATURE [Part::Fillet] Fillet004
  Base = -> Cut031
  Edges = 1 edges r=1.5: [Edge6]
FEATURE [Part::Cut] Cut032
  Base = -> Cut025
  Refine = true
  Tool = -> Cylinder080
FEATURE [Part::Cut] Cut033
  Base = -> Cut032
  Refine = true
  Tool = -> Cylinder079
FEATURE [Part::Chamfer] Chamfer004
  Base = -> Cut033
  Edges = 1 edges r=1.49: [Edge21]
FEATURE [Part::Chamfer] Chamfer003
  Base = -> Chamfer004
  Edges = 1 edges r=2: [Edge3]
FEATURE [Part::Fillet] Fillet005
  Base = -> Chamfer003
  Edges = 2 edges r=1.5: [Edge5,Edge19]
FEATURE [Part::MultiFuse] Fusion027  label="rim-wide-left"
  Placement = pos=(0,-88,0) rot=(-1,0,0;1.5708rad)
  Refine = true
  Shapes = -> [Fillet004,Fillet005]
FEATURE [Part::Cylinder] Cylinder058
  Angle = 360
  AttacherType = Attacher::AttachEngine3D
  Height = 6
  Placement = pos=(0,0,9) rot=(0,0,1;0rad)
  Radius = 15
FEATURE [Part::Cylinder] Cylinder103
  Angle = 360
  AttacherType = Attacher::AttachEngine3D
  Height = 1.5
  Placement = pos=(0,0,3) rot=(0,0,1;0rad)
  Radius = 7
FEATURE [Part::Cylinder] Cylinder060
  Angle = 360
  AttacherType = Attacher::AttachEngine3D
  Height = 4
  Placement = pos=(0,0,6.5) rot=(0,0,1;0rad)
  Radius = 5.6
FEATURE [Part::Cylinder] Cylinder061
  Angle = 360
  AttacherType = Attacher::AttachEngine3D
  Height = 4
  Radius = 5.6
FEATURE [Part::Cylinder] Cylinder062
  Angle = 360
  AttacherType = Attacher::AttachEngine3D
  Height = 4
  Placement = pos=(0,0,3) rot=(0,0,1;0rad)
  Radius = 3
FEATURE [Part::MultiFuse] Fusion033
  Placement = pos=(0,0,4.5) rot=(0,0,1;0rad)
  Refine = true
  Shapes = -> [Cylinder060,Cylinder062,Cylinder061]
FEATURE [Part::Cylinder] Cylinder104
  Angle = 360
  AttacherType = Attacher::AttachEngine3D
  Height = 20
  Placement = pos=(12.5,0,13) rot=(0,0,1;0rad)
  Radius = 0.8
FEATURE [Part::Cylinder] Cylinder105
  Angle = 360
  AttacherType = Attacher::AttachEngine3D
  Height = 20
  Placement = pos=(12.5,0,13) rot=(0,0,1;0rad)
  Radius = 0.8
FEATURE [Part::Cylinder] Cylinder106
  Angle = 360
  AttacherType = Attacher::AttachEngine3D
  Height = 20
  Placement = pos=(-12.5,0,13) rot=(0,0,1;0rad)
  Radius = 0.8
FEATURE [Part::MultiFuse] Fusion108
  Placement = pos=(0,0,0) rot=(0,0,1;1.5708rad)
  Refine = true
  Shapes = -> [Cylinder105,Cylinder106]
FEATURE [Part::Cylinder] Cylinder107
  Angle = 360
  AttacherType = Attacher::AttachEngine3D
  Height = 20
  Placement = pos=(12.5,0,13) rot=(0,0,1;0rad)
  Radius = 0.8
FEATURE [Part::Cylinder] Cylinder108
  Angle = 360
  AttacherType = Attacher::AttachEngine3D
  Height = 20
  Placement = pos=(-12.5,0,13) rot=(0,0,1;0rad)
  Radius = 0.8
FEATURE [Part::MultiFuse] Fusion105
  Placement = pos=(0,0,0) rot=(0,0,1;0.314159rad)
  Refine = true
  Shapes = -> [Cylinder104,Cylinder108]
FEATURE [Part::Cylinder] Cylinder109
  Angle = 360
  AttacherType = Attacher::AttachEngine3D
  Height = 6
  Placement = pos=(0,0,3) rot=(0,0,1;0rad)
  Radius = 10
FEATURE [Part::Cylinder] Cylinder110
  Angle = 360
  AttacherType = Attacher::AttachEngine3D
  Height = 20
  Placement = pos=(-12.5,0,13) rot=(0,0,1;0rad)
  Radius = 0.8
FEATURE [Part::MultiFuse] Fusion028
  Placement = pos=(0,0,0) rot=(0,0,1;0.942478rad)
  Refine = true
  Shapes = -> [Cylinder107,Cylinder110]
FEATURE [Part::Cylinder] Cylinder111
  Angle = 360
  AttacherType = Attacher::AttachEngine3D
  Height = 20
  Placement = pos=(12.5,0,13) rot=(0,0,1;0rad)
  Radius = 0.8
FEATURE [Part::Cylinder] Cylinder112
  Angle = 360
  AttacherType = Attacher::AttachEngine3D
  Height = 20
  Placement = pos=(-12.5,0,13) rot=(0,0,1;0rad)
  Radius = 0.8
FEATURE [Part::MultiFuse] Fusion106
  Placement = pos=(0,0,0) rot=(0,0,1;2.82743rad)
  Refine = true
  Shapes = -> [Cylinder111,Cylinder112]
FEATURE [Part::Cylinder] Cylinder113
  Angle = 360
  AttacherType = Attacher::AttachEngine3D
  Height = 20
  Placement = pos=(12.5,0,13) rot=(0,0,1;0rad)
  Radius = 0.8
FEATURE [Part::Cylinder] Cylinder114
  Angle = 360
  AttacherType = Attacher::AttachEngine3D
  Height = 20
  Placement = pos=(-12.5,0,13) rot=(0,0,1;0rad)
  Radius = 0.8
FEATURE [Part::MultiFuse] Fusion107
  Placement = pos=(0,0,0) rot=(0,0,1;2.19911rad)
  Refine = true
  Shapes = -> [Cylinder113,Cylinder114]
FEATURE [Part::MultiFuse] Fusion109
  Placement = pos=(0,0,3) rot=(0,0,1;0rad)
  Refine = true
  Shapes = -> [Fusion105,Fusion028,Fusion106,Fusion107,Fusion108]
FEATURE [Part::MultiFuse] Fusion110
  Refine = true
  Shapes = -> [Cylinder058,Cylinder109]
FEATURE [Part::Cut] Cut034
  Base = -> Fusion110
  Refine = true
  Tool = -> Cylinder103
FEATURE [Part::Cut] Cut035
  Base = -> Cut034
  Placement = pos=(0,0,8) rot=(0,0,1;0rad)
  Refine = true
  Tool = -> Fusion033
FEATURE [Part::Cut] Cut036
  Base = -> Cut035
  Refine = true
  Tool = -> Fusion109
FEATURE [Part::Cylinder] Cylinder115
  Angle = 360
  AttacherType = Attacher::AttachEngine3D
  Height = 3
  Placement = pos=(0,0,11) rot=(0,0,1;0rad)
  Radius = 10
FEATURE [Part::Cylinder] Cylinder116
  Angle = 360
  AttacherType = Attacher::AttachEngine3D
  Height = 3
  Placement = pos=(0,0,11) rot=(0,0,1;0rad)
  Radius = 8.5
FEATURE [Part::Cut] Cut037
  Base = -> Cylinder115
  Refine = true
  Tool = -> Cylinder116
FEATURE [Part::Cut] Cut038
  Base = -> Cut036
  Refine = true
  Tool = -> Cut037
FEATURE [Part::Chamfer] Chamfer002  label="hub-wide-left"
  Base = -> Cut038
  Edges = 1 edges r=1: [Edge1]
  Placement = pos=(0,-88,0) rot=(-1,0,0;1.5708rad)
FEATURE [Part::Cylinder] Cylinder117
  Angle = 360
  AttacherType = Attacher::AttachEngine3D
  Height = 3
  Placement = pos=(0,0,11) rot=(0,0,1;0rad)
  Radius = 10
FEATURE [Part::Cylinder] Cylinder118
  Angle = 360
  AttacherType = Attacher::AttachEngine3D
  Height = 7
  Placement = pos=(0,0,7) rot=(0,0,1;0rad)
  Radius = 8.55
FEATURE [Part::Cone] Cone
  Angle = 360
  AttacherType = Attacher::AttachEngine3D
  Height = 8
  Placement = pos=(0,0,3) rot=(0,0,1;0rad)
  Radius1 = 6
  Radius2 = 10
FEATURE [Part::MultiFuse] Fusion111
  Refine = true
  Shapes = -> [Cone,Cylinder117]
FEATURE [Part::Chamfer] Chamfer005
  Base = -> Cylinder118
  Edges = 1 edges r=2: [Edge3]
FEATURE [Part::Cylinder] Cylinder119
  Angle = 360
  AttacherType = Attacher::AttachEngine3D
  Height = 7
  Placement = pos=(0,0,5) rot=(0,0,1;0rad)
  Radius = 5
FEATURE [Part::MultiFuse] Fusion112
  Refine = true
  Shapes = -> [Chamfer005,Cylinder119]
FEATURE [Part::Cut] Cut039
  Base = -> Fusion111
  Refine = true
  Tool = -> Fusion112
FEATURE [Part::Chamfer] Chamfer006  label="hub-wide-cap_"
  Base = -> Cut039
  Edges = 1 edges r=1.54: [Edge11]
FEATURE [Part::Fillet] Fillet006  label="hub-wide-cap-left"
  Base = -> Chamfer006
  Edges = 2 edges r=1: [Edge13,Edge15]
  Placement = pos=(0,-88,0) rot=(-1,0,0;1.5708rad)
FEATURE [Part::Cylinder] Cylinder120
  Angle = 360
  AttacherType = Attacher::AttachEngine3D
  Height = 15
  Placement = pos=(13.5,49.5,13) rot=(0,0,1;0rad)
  Radius = 1.75
FEATURE [Part::Cylinder] Cylinder121
  Angle = 360
  AttacherType = Attacher::AttachEngine3D
  Height = 15
  Placement = pos=(13.5,-49.5,13) rot=(0,0,1;0rad)
  Radius = 1.75
FEATURE [Part::Cylinder] Cylinder122
  Angle = 360
  AttacherType = Attacher::AttachEngine3D
  Height = 6
  Placement = pos=(0,0,9) rot=(0,0,1;0rad)
  Radius = 15
FEATURE [Part::Cylinder] Cylinder123
  Angle = 360
  AttacherType = Attacher::AttachEngine3D
  Height = 1.5
  Placement = pos=(0,0,3) rot=(0,0,1;0rad)
  Radius = 7
FEATURE [Part::Cylinder] Cylinder124
  Angle = 360
  AttacherType = Attacher::AttachEngine3D
  Height = 4
  Placement = pos=(0,0,6.5) rot=(0,0,1;0rad)
  Radius = 5.6
FEATURE [Part::Cylinder] Cylinder125
  Angle = 360
  AttacherType = Attacher::AttachEngine3D
  Height = 4
  Radius = 5.6
FEATURE [Part::Cylinder] Cylinder126
  Angle = 360
  AttacherType = Attacher::AttachEngine3D
  Height = 4
  Placement = pos=(0,0,3) rot=(0,0,1;0rad)
  Radius = 3
FEATURE [Part::MultiFuse] Fusion116
  Placement = pos=(0,0,4.5) rot=(0,0,1;0rad)
  Refine = true
  Shapes = -> [Cylinder124,Cylinder126,Cylinder125]
FEATURE [Part::Cylinder] Cylinder127
  Angle = 360
  AttacherType = Attacher::AttachEngine3D
  Height = 20
  Placement = pos=(12.5,0,13) rot=(0,0,1;0rad)
  Radius = 0.8
FEATURE [Part::Cylinder] Cylinder128
  Angle = 360
  AttacherType = Attacher::AttachEngine3D
  Height = 20
  Placement = pos=(12.5,0,13) rot=(0,0,1;0rad)
  Radius = 0.8
FEATURE [Part::Cylinder] Cylinder129
  Angle = 360
  AttacherType = Attacher::AttachEngine3D
  Height = 20
  Placement = pos=(-12.5,0,13) rot=(0,0,1;0rad)
  Radius = 0.8
FEATURE [Part::MultiFuse] Fusion118
  Placement = pos=(0,0,0) rot=(0,0,1;1.5708rad)
  Refine = true
  Shapes = -> [Cylinder128,Cylinder129]
FEATURE [Part::Cylinder] Cylinder130
  Angle = 360
  AttacherType = Attacher::AttachEngine3D
  Height = 20
  Placement = pos=(12.5,0,13) rot=(0,0,1;0rad)
  Radius = 0.8
FEATURE [Part::Cylinder] Cylinder131
  Angle = 360
  AttacherType = Attacher::AttachEngine3D
  Height = 20
  Placement = pos=(-12.5,0,13) rot=(0,0,1;0rad)
  Radius = 0.8
FEATURE [Part::MultiFuse] Fusion114
  Placement = pos=(0,0,0) rot=(0,0,1;0.314159rad)
  Refine = true
  Shapes = -> [Cylinder127,Cylinder131]
FEATURE [Part::Cylinder] Cylinder132
  Angle = 360
  AttacherType = Attacher::AttachEngine3D
  Height = 6
  Placement = pos=(0,0,3) rot=(0,0,1;0rad)
  Radius = 10
FEATURE [Part::Cylinder] Cylinder133
  Angle = 360
  AttacherType = Attacher::AttachEngine3D
  Height = 20
  Placement = pos=(-12.5,0,13) rot=(0,0,1;0rad)
  Radius = 0.8
FEATURE [Part::MultiFuse] Fusion113
  Placement = pos=(0,0,0) rot=(0,0,1;0.942478rad)
  Refine = true
  Shapes = -> [Cylinder130,Cylinder133]
FEATURE [Part::Cylinder] Cylinder134
  Angle = 360
  AttacherType = Attacher::AttachEngine3D
  Height = 20
  Placement = pos=(12.5,0,13) rot=(0,0,1;0rad)
  Radius = 0.8
FEATURE [Part::Cylinder] Cylinder135
  Angle = 360
  AttacherType = Attacher::AttachEngine3D
  Height = 20
  Placement = pos=(-12.5,0,13) rot=(0,0,1;0rad)
  Radius = 0.8
FEATURE [Part::MultiFuse] Fusion115
  Placement = pos=(0,0,0) rot=(0,0,1;2.82743rad)
  Refine = true
  Shapes = -> [Cylinder134,Cylinder135]
FEATURE [Part::Cylinder] Cylinder136
  Angle = 360
  AttacherType = Attacher::AttachEngine3D
  Height = 20
  Placement = pos=(12.5,0,13) rot=(0,0,1;0rad)
  Radius = 0.8
FEATURE [Part::Cylinder] Cylinder137
  Angle = 360
  AttacherType = Attacher::AttachEngine3D
  Height = 20
  Placement = pos=(-12.5,0,13) rot=(0,0,1;0rad)
  Radius = 0.8
FEATURE [Part::MultiFuse] Fusion117
  Placement = pos=(0,0,0) rot=(0,0,1;2.19911rad)
  Refine = true
  Shapes = -> [Cylinder136,Cylinder137]
FEATURE [Part::MultiFuse] Fusion119
  Placement = pos=(0,0,3) rot=(0,0,1;0rad)
  Refine = true
  Shapes = -> [Fusion114,Fusion113,Fusion115,Fusion117,Fusion118]
FEATURE [Part::MultiFuse] Fusion120
  Refine = true
  Shapes = -> [Cylinder122,Cylinder132]
FEATURE [Part::Cut] Cut040
  Base = -> Fusion120
  Refine = true
  Tool = -> Cylinder123
FEATURE [Part::Cut] Cut041
  Base = -> Cut040
  Placement = pos=(0,0,8) rot=(0,0,1;0rad)
  Refine = true
  Tool = -> Fusion116
FEATURE [Part::Cut] Cut042
  Base = -> Cut041
  Refine = true
  Tool = -> Fusion119
FEATURE [Part::Cylinder] Cylinder138
  Angle = 360
  AttacherType = Attacher::AttachEngine3D
  Height = 3
  Placement = pos=(0,0,11) rot=(0,0,1;0rad)
  Radius = 10
FEATURE [Part::Cylinder] Cylinder139
  Angle = 360
  AttacherType = Attacher::AttachEngine3D
  Height = 3
  Placement = pos=(0,0,11) rot=(0,0,1;0rad)
  Radius = 8.5
FEATURE [Part::Cut] Cut043
  Base = -> Cylinder138
  Refine = true
  Tool = -> Cylinder139
FEATURE [Part::Cut] Cut044
  Base = -> Cut042
  Refine = true
  Tool = -> Cut043
FEATURE [Part::Chamfer] Chamfer007  label="hub-wide-right"
  Base = -> Cut044
  Edges = 1 edges r=1: [Edge1]
  Placement = pos=(0,88,0) rot=(1,0,0;1.5708rad)
FEATURE [Part::MultiFuse] Fusion121
  Refine = true
  Shapes = -> [Cylinder120,Cylinder121]
FEATURE [Part::Cylinder] Cylinder140
  Angle = 360
  AttacherType = Attacher::AttachEngine3D
  Height = 15
  Placement = pos=(13.5,-49.5,13) rot=(0,0,1;0rad)
  Radius = 1.75
FEATURE [Part::Cylinder] Cylinder141
  Angle = 360
  AttacherType = Attacher::AttachEngine3D
  Height = 15
  Placement = pos=(13.5,49.5,13) rot=(0,0,1;0rad)
  Radius = 1.75
FEATURE [Part::MultiFuse] Fusion122
  Placement = pos=(-12,0,0) rot=(0,0,1;0rad)
  Refine = true
  Shapes = -> [Cylinder141,Cylinder140]
FEATURE [Part::MultiFuse] Fusion123
  Placement = pos=(-7.5,0,-20.5) rot=(0,0,1;0rad)
  Refine = true
  Shapes = -> [Fusion122,Fusion121]
FEATURE [Part::Cylinder] Cylinder142
  Angle = 360
  AttacherType = Attacher::AttachEngine3D
  Height = 128
  Placement = pos=(0,-64,0) rot=(-1,0,0;1.5708rad)
  Radius = 8
FEATURE [Part::Box] Box011  label="Cube"
  AttacherType = Attacher::AttachEngine3D
  Height = 15
  Length = 20
  Placement = pos=(-10,-53.5,-7.5) rot=(0,0,1;0rad)
  Width = 8
FEATURE [Part::Fillet] Fillet007
  Base = -> Box011
  Edges = 4 edges r=3: [Edge1,Edge3,Edge5,Edge7]
  Placement = pos=(0,99,0) rot=(0,0,1;0rad)
FEATURE [Part::Box] Box012  label="Cube001"
  AttacherType = Attacher::AttachEngine3D
  Height = 15
  Length = 20
  Placement = pos=(-10,-53.5,-7.5) rot=(0,0,1;0rad)
  Width = 8
FEATURE [Part::Fillet] Fillet008
  Base = -> Box012
  Edges = 4 edges r=3: [Edge1,Edge3,Edge5,Edge7]
FEATURE [Part::Cylinder] Cylinder143
  Angle = 360
  AttacherType = Attacher::AttachEngine3D
  Height = 128
  Placement = pos=(0,-64,0) rot=(-1,0,0;1.5708rad)
  Radius = 2.55
FEATURE [Part::Cylinder] Cylinder144
  Angle = 360
  AttacherType = Attacher::AttachEngine3D
  Height = 4
  Placement = pos=(0,-64,0) rot=(-1,0,0;1.5708rad)
  Radius = 5.6
FEATURE [Part::Cylinder] Cylinder145
  Angle = 360
  AttacherType = Attacher::AttachEngine3D
  Height = 4
  Placement = pos=(0,60,0) rot=(-1,0,0;1.5708rad)
  Radius = 5.6
FEATURE [Part::MultiFuse] Fusion124
  Refine = true
  Shapes = -> [Cylinder145,Cylinder144]
FEATURE [Part::MultiFuse] Fusion125
  Refine = true
  Shapes = -> [Cylinder143,Fusion124]
FEATURE [Part::MultiFuse] Fusion126
  Refine = true
  Shapes = -> [Cylinder142,Fillet008,Fillet007]
FEATURE [Part::Box] Box013  label="Cube002"
  AttacherType = Attacher::AttachEngine3D
  Height = 1
  Length = 20
  Placement = pos=(-10,-64,-8.5) rot=(0,0,1;0rad)
  Width = 128
FEATURE [Part::Box] Box014  label="Cube003"
  AttacherType = Attacher::AttachEngine3D
  Height = 1
  Length = 20
  Placement = pos=(-10,-64,7.5) rot=(0,0,1;0rad)
  Width = 128
FEATURE [Part::MultiFuse] Fusion127
  Refine = true
  Shapes = -> [Box013,Box014]
FEATURE [Part::Cylinder] Cylinder148
  Angle = 360
  AttacherType = Attacher::AttachEngine3D
  Height = 6
  Placement = pos=(0,0,-7.5) rot=(0,0,1;0rad)
  Radius = 1.5
FEATURE [Part::Cylinder] Cylinder149
  Angle = 360
  AttacherType = Attacher::AttachEngine3D
  Height = 25
  Placement = pos=(0,-30,0) rot=(-1,0,0;1.5708rad)
  Radius = 2.8
FEATURE [Part::Cylinder] Cylinder150
  Angle = 360
  AttacherType = Attacher::AttachEngine3D
  Height = 25
  Placement = pos=(0,5,0) rot=(-1,0,0;1.5708rad)
  Radius = 2.8
FEATURE [Part::MultiFuse] Fusion128
  Refine = true
  Shapes = -> [Cylinder150,Cylinder149]
FEATURE [Part::Box] Box015  label="Cube004"
  AttacherType = Attacher::AttachEngine3D
  Height = 15
  Length = 5.5
  Placement = pos=(2.5,-30,-7.5) rot=(0,0,1;0rad)
  Width = 6
FEATURE [Part::Box] Box016  label="Cube005"
  AttacherType = Attacher::AttachEngine3D
  Height = 15
  Length = 5.5
  Placement = pos=(2.5,24,-7.5) rot=(0,0,1;0rad)
  Width = 6
FEATURE [Part::MultiFuse] Fusion129
  Refine = true
  Shapes = -> [Box016,Box015]
FEATURE [Part::Fillet] Fillet009
  Base = -> Fusion129
  Edges = 8 edges r=2: [Edge9,Edge10,Edge11,Edge12,Edge21,Edge22,Edge23,Edge24]
FEATURE [Part::MultiFuse] Fusion130
  Refine = true
  Shapes = -> [Fusion126,Fillet009]
FEATURE [Part::Cylinder] Cylinder151
  Angle = 360
  AttacherType = Attacher::AttachEngine3D
  Height = 10
  Placement = pos=(0,-27,4.5) rot=(0,1,0;1.5708rad)
  Radius = 1.25
FEATURE [Part::Cylinder] Cylinder152
  Angle = 360
  AttacherType = Attacher::AttachEngine3D
  Height = 10
  Placement = pos=(0,-27,-4.5) rot=(0,1,0;1.5708rad)
  Radius = 1.25
FEATURE [Part::MultiFuse] Fusion131
  Refine = true
  Shapes = -> [Cylinder152,Cylinder151]
FEATURE [Part::Cylinder] Cylinder153
  Angle = 360
  AttacherType = Attacher::AttachEngine3D
  Height = 10
  Placement = pos=(0,-27,4.5) rot=(0,1,0;1.5708rad)
  Radius = 1.25
FEATURE [Part::Cylinder] Cylinder154
  Angle = 360
  AttacherType = Attacher::AttachEngine3D
  Height = 10
  Placement = pos=(0,-27,-4.5) rot=(0,1,0;1.5708rad)
  Radius = 1.25
FEATURE [Part::MultiFuse] Fusion132
  Placement = pos=(0,54,0) rot=(0,0,1;0rad)
  Refine = true
  Shapes = -> [Cylinder154,Cylinder153]
FEATURE [Part::MultiFuse] Fusion133
  Placement = pos=(-2,0,0) rot=(0,0,1;0rad)
  Refine = true
  Shapes = -> [Fusion132,Fusion131]
FEATURE [Part::Cut] Cut045
  Base = -> Fusion130
  Refine = true
  Tool = -> Fusion125
FEATURE [Part::Cut] Cut046
  Base = -> Cut045
  Refine = true
  Tool = -> Fusion133
FEATURE [Part::Cut] Cut047
  Base = -> Cut046
  Refine = true
  Tool = -> Fusion123
FEATURE [Part::Cut] Cut048
  Base = -> Cut047
  Refine = true
  Tool = -> Fusion128
FEATURE [Part::Cut] Cut049
  Base = -> Cut048
  Refine = true
  Tool = -> Fusion127
FEATURE [Part::Cut] Cut050  label="axle-wide"
  Base = -> Cut049
  Refine = true
  Tool = -> Cylinder148
FEATURE [Part::Fillet] Fillet
  Base = -> Cut019
  Edges = 2 edges r=2: [Edge1,Edge3]
FEATURE [Part::Chamfer] Chamfer
  Base = -> Fillet
  Edges = 2 edges r=4: [Edge8,Edge9]
FEATURE [Part::Fillet] Fillet010  label="wheel-wide-left"
  Base = -> Chamfer
  Edges = 2 edges r=3: [Edge1,Edge12]
  Placement = pos=(0,-63,0) rot=(0,0,1;0rad)
